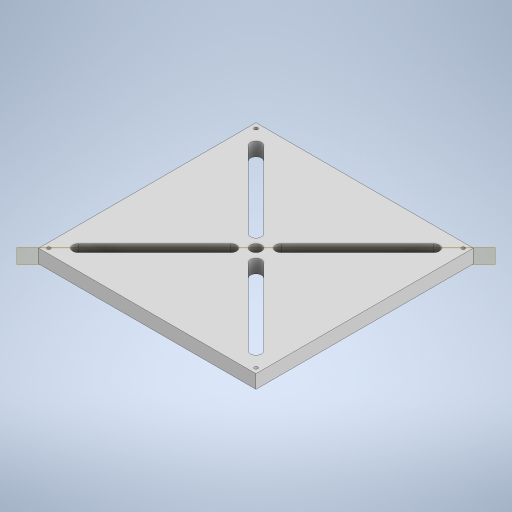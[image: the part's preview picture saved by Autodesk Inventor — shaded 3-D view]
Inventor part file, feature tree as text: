
AUTODESK INVENTOR PART (.ipt)
format: ipt  version: 2024 (Build 280153000, 153)  size: 316,416 bytes
history: native  units: in
note: dims shown in document units (in); Inventor stores cm internally (conversion verified against a paired STEP export)
features: projected_geometry x3, extrude x2, sketch x1, plane x1
ambient origin geometry x8: Origin, YZ Plane, XZ Plane, XY Plane, X Axis, Y Axis, Z Axis, Center Point
bodies: Solid1 (feature_tree)
feature tree (7):
  extrude  "Extrusion1"  Depth=4.0in
  extrude  "Extrusion2"  Depth=0.25in
  sketch  "Sketch4"  dims[d0=4.0in d1=4.0in d2=0.1875in d11=0.25in d12=0.0in d20=0.0625in d21=0.0938in d22=0.0938in d23=0.7874in d25=3.8125in d26=0.7874in d28=3.8125in d31=0.25in d32=0.0in d33=0.201in d34=0.125in d35=0.2in d36=0.25in d37=1.5748in d39=360.0deg d41=0.17in d42=2.0in d43=0.17in d44=0.17in d45=1.5in d46=1.5in]
  plane  "Work Plane1"
  projected_geometry  "Projected Loop1"
  projected_geometry  "Projected Loop2"
  projected_geometry  "Projected Loop3"
